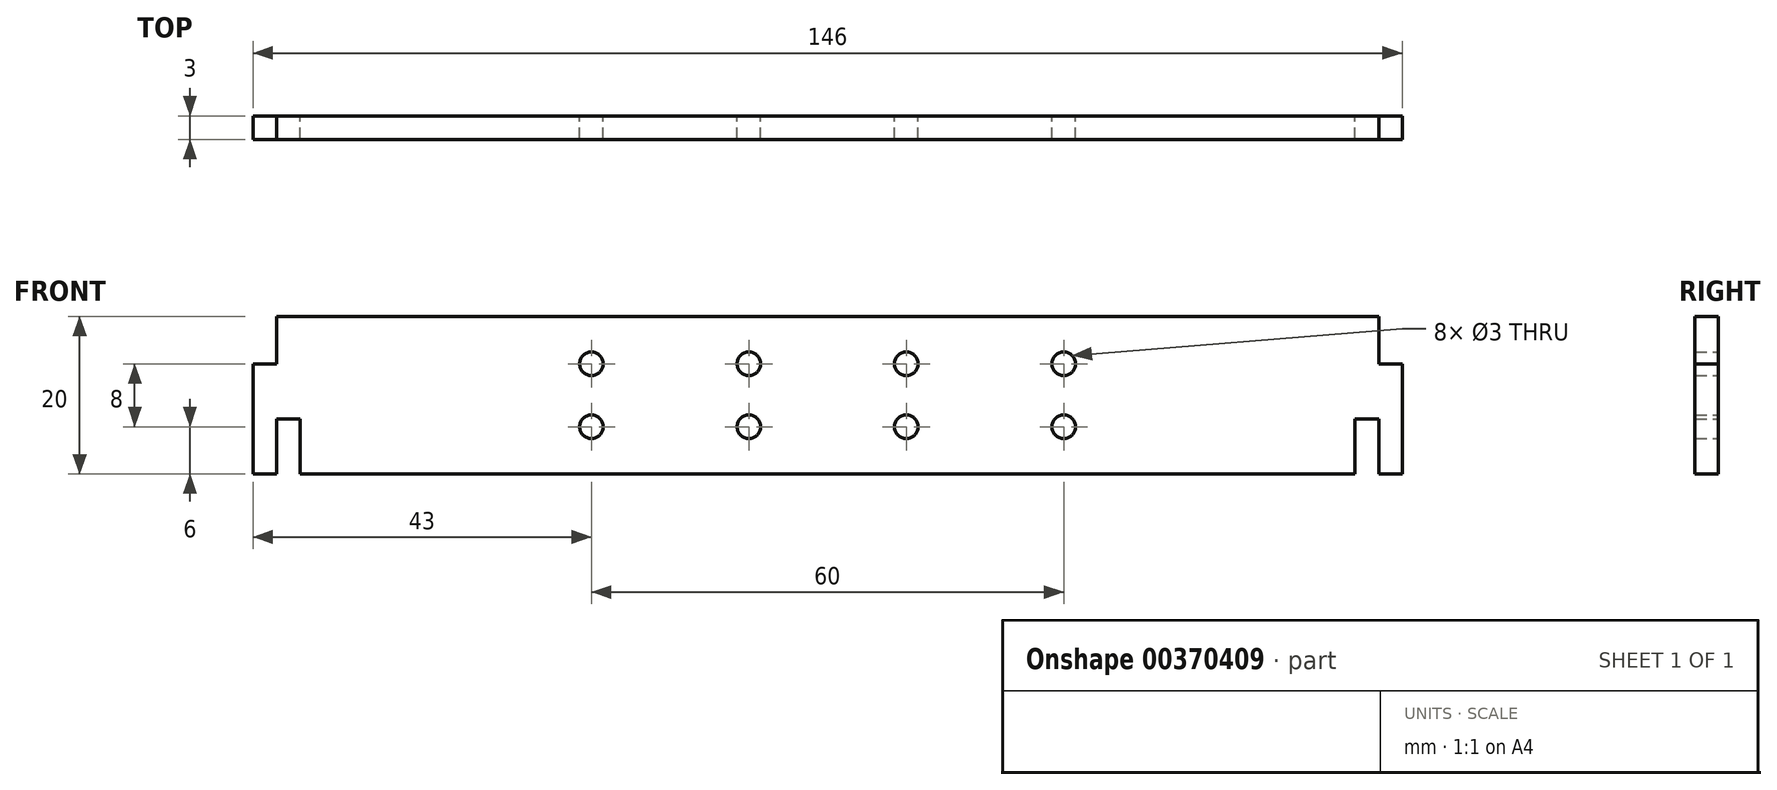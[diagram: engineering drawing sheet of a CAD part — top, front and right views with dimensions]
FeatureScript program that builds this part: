
annotation { "Feature Type Name" : "Feature", "Feature Type Description" : "" }
export const myFeature = defineFeature(function(context is Context, id is Id, definition is map)
    precondition{}
    {
        {
            var Q0;
            Q0=qCreatedBy(makeId("Front.planeOp"),FACE);
            var sketch = newSketch(context, id + "F0", { "sketchPlane" : qUnion([Q0])});
            skLineSegment(sketch, "E0", {"start": v(0, 0) * mm, "end": v(70, 0) * mm});
            skLineSegment(sketch, "E1", {"start": v(70, 0) * mm, "end": v(70, -6) * mm});
            skLineSegment(sketch, "E2", {"start": v(70, -6) * mm, "end": v(73, -6) * mm});
            skLineSegment(sketch, "E3", {"start": v(73, -6) * mm, "end": v(73, -20) * mm});
            skLineSegment(sketch, "E4", {"start": v(73, -20) * mm, "end": v(70, -20) * mm});
            skLineSegment(sketch, "E5", {"start": v(70, -20) * mm, "end": v(70, -13) * mm});
            skLineSegment(sketch, "E6", {"start": v(70, -13) * mm, "end": v(67, -13) * mm});
            skLineSegment(sketch, "E7", {"start": v(67, -13) * mm, "end": v(67, -20) * mm});
            skLineSegment(sketch, "E8", {"start": v(67, -20) * mm, "end": v(0, -20) * mm});
            skLineSegment(sketch, "E9.MirrorCS", {"start": v(-70, -6) * mm, "end": v(-73, -6) * mm});
            skLineSegment(sketch, "E10.MirrorCS", {"start": v(-70, -13) * mm, "end": v(-67, -13) * mm});
            skLineSegment(sketch, "E11.MirrorCS", {"start": v(-73, -20) * mm, "end": v(-70, -20) * mm});
            skLineSegment(sketch, "E12.MirrorCS", {"start": v(-67, -13) * mm, "end": v(-67, -20) * mm});
            skLineSegment(sketch, "E13.MirrorCS", {"start": v(-73, -6) * mm, "end": v(-73, -20) * mm});
            skLineSegment(sketch, "E14.MirrorCS", {"start": v(-70, -20) * mm, "end": v(-70, -13) * mm});
            skLineSegment(sketch, "E15.MirrorCS", {"start": v(-67, -20) * mm, "end": v(0, -20) * mm});
            skLineSegment(sketch, "E16.MirrorCS", {"start": v(0, 0) * mm, "end": v(-70, 0) * mm});
            skLineSegment(sketch, "E17.MirrorCS", {"start": v(-70, 0) * mm, "end": v(-70, -6) * mm});
            skCircle(sketch, "E18", {"center": v(10, -6) * mm, "radius": 1.5 * mm});
            skCircle(sketch, "E19", {"center": v(10, -14) * mm, "radius": 1.5 * mm});
            skCircle(sketch, "E20", {"center": v(30, -6) * mm, "radius": 1.5 * mm});
            skCircle(sketch, "E21", {"center": v(30, -14) * mm, "radius": 1.5 * mm});
            skCircle(sketch, "E22.MirrorC", {"center": v(-10, -6) * mm, "radius": 1.5 * mm});
            skCircle(sketch, "E23.MirrorC", {"center": v(-10, -14) * mm, "radius": 1.5 * mm});
            skCircle(sketch, "E24.MirrorC", {"center": v(-30, -14) * mm, "radius": 1.5 * mm});
            skCircle(sketch, "E25.MirrorC", {"center": v(-30, -6) * mm, "radius": 1.5 * mm});
            skSolve(sketch);
        }
        {
            var Q0;
            Q0=makeQuery(id+"F0.imprint","IMPRINT",FACE,{"disambiguationData":[TD([[makeQuery(id+"F0.imprint","IMPRINT",EDGE,{"derivedFrom":sQuery(id+"F0.wireOp",EDGE,"E0")}),-1.0]])]});
            extrude(context, id + "F1", {"entities" : qUnion([Q0]), "depth" : 3 * mm});
        }
    });
